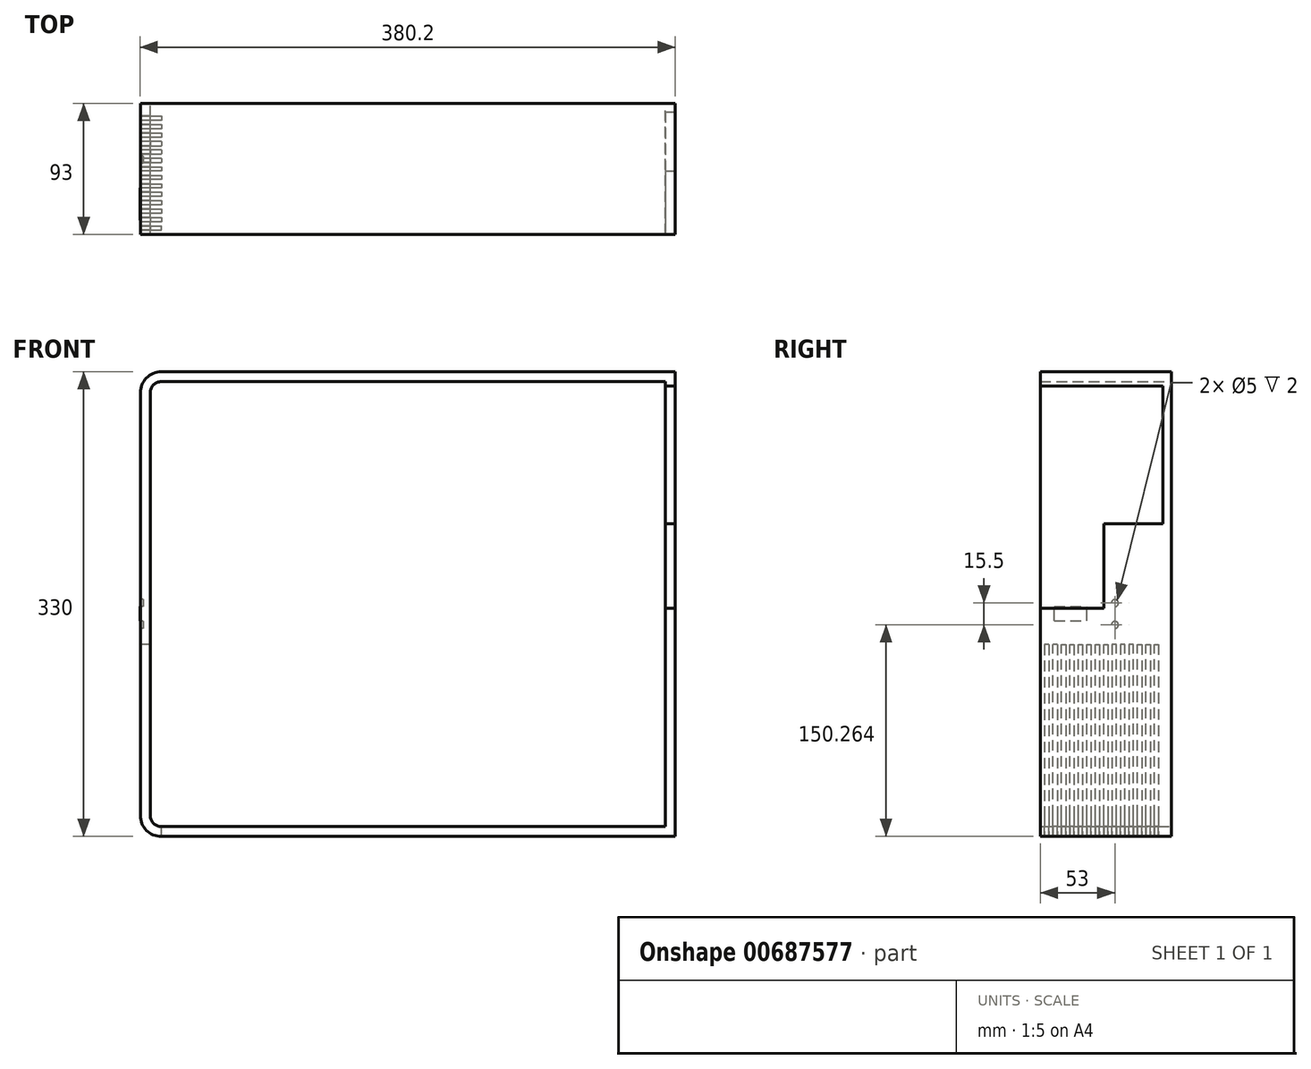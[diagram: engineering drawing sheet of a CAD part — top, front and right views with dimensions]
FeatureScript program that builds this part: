
annotation { "Feature Type Name" : "Feature", "Feature Type Description" : "" }
export const myFeature = defineFeature(function(context is Context, id is Id, definition is map)
    precondition{}
    {
        {
            var Q0;
            Q0=qCreatedBy(makeId("Front.planeOp"),FACE);
            var sketch = newSketch(context, id + "F0", { "sketchPlane" : qUnion([Q0])});
            skLineSegment(sketch, "E0.bottom", {"start": v(-173.8, 236.53) * mm, "end": v(191.2, 236.53) * mm});
            skLineSegment(sketch, "E0.top", {"start": v(-173.8, -93.47) * mm, "end": v(191.2, -93.47) * mm});
            skLineSegment(sketch, "E0.left", {"start": v(-188.8, 221.53) * mm, "end": v(-188.8, -78.47) * mm});
            skLineSegment(sketch, "E0.right", {"start": v(191.2, 236.53) * mm, "end": v(191.2, -93.47) * mm});
            skPoint(sketch, "E1.visualSharp", {"position": v(-188.8, 236.53) * mm});
            skArc(sketch, "E1.filletArc", {"start": v(-186.8, 236.53) * mm, "mid": v(-188.22, 235.95) * mm, "end": v(-188.8, 234.53) * mm});
            skArc(sketch, "E2.filletArc", {"start": v(-173.8, 236.53) * mm, "mid": v(-184.41, 232.14) * mm, "end": v(-188.8, 221.53) * mm});
            skPoint(sketch, "E3.visualSharp", {"position": v(-188.8, -93.47) * mm});
            skArc(sketch, "E3.filletArc", {"start": v(-188.8, -78.47) * mm, "mid": v(-184.41, -89.07) * mm, "end": v(-173.8, -93.47) * mm});
            skArc(sketch, "E4.0", {"start": v(-173.8, 229.53) * mm, "mid": v(-179.46, 227.19) * mm, "end": v(-181.8, 221.53) * mm});
            skLineSegment(sketch, "E4.1", {"start": v(184.2, 229.53) * mm, "end": v(184.2, -86.47) * mm});
            skLineSegment(sketch, "E4.2", {"start": v(-173.8, -86.47) * mm, "end": v(184.2, -86.47) * mm});
            skLineSegment(sketch, "E4.3", {"start": v(-173.8, 229.53) * mm, "end": v(184.2, 229.53) * mm});
            skArc(sketch, "E4.4", {"start": v(-181.8, -78.47) * mm, "mid": v(-179.46, -84.12) * mm, "end": v(-173.8, -86.47) * mm});
            skLineSegment(sketch, "E4.5", {"start": v(-181.8, 221.53) * mm, "end": v(-181.8, -78.47) * mm});
            skSolve(sketch);
        }
        {
            var Q0;
            Q0 = qSketchRegion(id + "F0", true);
            extrude(context, id + "F1", {"entities" : qUnion([Q0]), "depth" : 93 * mm, "offsetDistance" : 25 * mm});
        }
        {
            var Q0;
            Q0=makeQuery(id+"F1.opExtrude","SWEPT_FACE",FACE,{"disambiguationData":[OSD([sQuery(id+"F0.wireOp",EDGE,"E0.right")])]});
            var sketch = newSketch(context, id + "F2", { "sketchPlane" : qUnion([Q0])});
            skLineSegment(sketch, "E5", {"start": v(-6, 226.53) * mm, "end": v(-6, 128.46) * mm});
            skPoint(sketch, "E6.orphan", {"position": v(-6, 236.53) * mm});
            skLineSegment(sketch, "E7", {"start": v(-6, 128.46) * mm, "end": v(-48, 128.46) * mm});
            skLineSegment(sketch, "E8", {"start": v(-48, 128.46) * mm, "end": v(-48, 68.46) * mm});
            skLineSegment(sketch, "E9", {"start": v(-48, 68.46) * mm, "end": v(-93, 68.46) * mm});
            skLineSegment(sketch, "E10", {"start": v(-6, 226.53) * mm, "end": v(-93, 226.53) * mm});
            skSolve(sketch);
        }
        {
            var Q0;
            Q0 = qSketchRegion(id + "F2", true);
            var Q1;
            Q1=makeQuery(id+"F2.imprint","IMPRINT",FACE,{"disambiguationData":[TD([[makeQuery(id+"F2.imprint","IMPRINT",EDGE,{"derivedFrom":sQuery(id+"F2.wireOp",EDGE,"E5")}),-1.0]])]});
            extrude(context, id + "F3", {"entities" : qUnion([Q0, Q1]), "operationType" : NewBodyOperationType.REMOVE, "oppositeDirection" : true, "depth" : 25 * mm, "offsetDistance" : 25 * mm});
        }
        {
            var Q0;
            Q0=makeQuery(id+"F1.opExtrude","SWEPT_FACE",FACE,{"disambiguationData":[OSD([sQuery(id+"F0.wireOp",EDGE,"E0.left")])]});
            var sketch = newSketch(context, id + "F4", { "sketchPlane" : qUnion([Q0])});
            skLineSegment(sketch, "E11", {"start": v(90, -94.2) * mm, "end": v(90, 42.8) * mm});
            skLineSegment(sketch, "E12", {"start": v(87, -94.2) * mm, "end": v(87, 42.8) * mm});
            skLineSegment(sketch, "E13", {"start": v(84, 42.8) * mm, "end": v(84, -94.2) * mm});
            skLineSegment(sketch, "E14", {"start": v(81, -94.2) * mm, "end": v(81, 42.8) * mm});
            skLineSegment(sketch, "E15", {"start": v(78, 42.8) * mm, "end": v(78, -94.2) * mm});
            skLineSegment(sketch, "E16", {"start": v(75, -94.2) * mm, "end": v(75, 42.8) * mm});
            skLineSegment(sketch, "E17", {"start": v(72, 42.8) * mm, "end": v(72, -94.2) * mm});
            skLineSegment(sketch, "E18", {"start": v(69, -94.2) * mm, "end": v(69, 42.8) * mm});
            skLineSegment(sketch, "E19", {"start": v(90, 42.8) * mm, "end": v(87, 42.8) * mm});
            skLineSegment(sketch, "E20", {"start": v(84, 42.8) * mm, "end": v(81, 42.8) * mm});
            skLineSegment(sketch, "E21", {"start": v(90, -94.2) * mm, "end": v(87, -94.2) * mm});
            skLineSegment(sketch, "E22", {"start": v(81, -94.2) * mm, "end": v(84, -94.2) * mm});
            skLineSegment(sketch, "E23", {"start": v(78, -94.2) * mm, "end": v(75, -94.2) * mm});
            skLineSegment(sketch, "E24", {"start": v(72, -94.2) * mm, "end": v(69, -94.2) * mm});
            skLineSegment(sketch, "E25", {"start": v(66, 42.8) * mm, "end": v(66, -94.2) * mm});
            skLineSegment(sketch, "E26", {"start": v(66, -94.2) * mm, "end": v(63, -94.2) * mm});
            skLineSegment(sketch, "E27", {"start": v(63, -94.2) * mm, "end": v(63, 42.8) * mm});
            skLineSegment(sketch, "E28", {"start": v(63, 42.8) * mm, "end": v(66, 42.8) * mm});
            skLineSegment(sketch, "E29", {"start": v(60, 42.8) * mm, "end": v(60, -94.2) * mm});
            skLineSegment(sketch, "E30", {"start": v(60, -94.2) * mm, "end": v(57, -94.2) * mm});
            skLineSegment(sketch, "E31", {"start": v(57, -94.2) * mm, "end": v(57, 42.8) * mm});
            skLineSegment(sketch, "E32", {"start": v(57, 42.8) * mm, "end": v(60, 42.8) * mm});
            skLineSegment(sketch, "E33", {"start": v(54, 42.8) * mm, "end": v(54, -94.2) * mm});
            skLineSegment(sketch, "E34", {"start": v(54, -94.2) * mm, "end": v(51, -94.2) * mm});
            skLineSegment(sketch, "E35", {"start": v(51, -94.2) * mm, "end": v(51, 42.8) * mm});
            skLineSegment(sketch, "E36", {"start": v(51, 42.8) * mm, "end": v(54, 42.8) * mm});
            skLineSegment(sketch, "E37", {"start": v(48, 42.93) * mm, "end": v(48, -94.2) * mm});
            skLineSegment(sketch, "E38", {"start": v(48, -94.2) * mm, "end": v(45, -94.2) * mm});
            skLineSegment(sketch, "E39", {"start": v(45, -94.2) * mm, "end": v(45, 42.93) * mm});
            skLineSegment(sketch, "E40", {"start": v(45, 42.93) * mm, "end": v(48, 42.93) * mm});
            skLineSegment(sketch, "E41", {"start": v(42, 42.93) * mm, "end": v(39, 42.93) * mm});
            skLineSegment(sketch, "E42", {"start": v(39, 42.93) * mm, "end": v(39, -94.2) * mm});
            skLineSegment(sketch, "E43", {"start": v(39, -94.2) * mm, "end": v(42, -94.2) * mm});
            skLineSegment(sketch, "E44", {"start": v(42, -94.2) * mm, "end": v(42, 42.93) * mm});
            skLineSegment(sketch, "E45", {"start": v(36, 42.93) * mm, "end": v(33, 42.93) * mm});
            skLineSegment(sketch, "E46", {"start": v(33, 42.93) * mm, "end": v(33, -94.2) * mm});
            skLineSegment(sketch, "E47", {"start": v(33, -94.2) * mm, "end": v(36, -94.2) * mm});
            skLineSegment(sketch, "E48", {"start": v(36, -94.2) * mm, "end": v(36, 42.93) * mm});
            skLineSegment(sketch, "E49", {"start": v(30, 42.93) * mm, "end": v(27, 42.93) * mm});
            skLineSegment(sketch, "E50", {"start": v(27, 42.93) * mm, "end": v(27, -94.2) * mm});
            skLineSegment(sketch, "E51", {"start": v(27, -94.2) * mm, "end": v(30, -94.2) * mm});
            skLineSegment(sketch, "E52", {"start": v(30, -94.2) * mm, "end": v(30, 42.93) * mm});
            skLineSegment(sketch, "E53", {"start": v(24, 42.93) * mm, "end": v(24, -94.2) * mm});
            skLineSegment(sketch, "E54", {"start": v(24, -94.2) * mm, "end": v(21, -94.2) * mm});
            skLineSegment(sketch, "E55", {"start": v(21, -94.2) * mm, "end": v(21, 42.93) * mm});
            skLineSegment(sketch, "E56", {"start": v(21, 42.93) * mm, "end": v(24, 42.93) * mm});
            skLineSegment(sketch, "E57", {"start": v(18, 42.93) * mm, "end": v(18, -94.2) * mm});
            skLineSegment(sketch, "E58", {"start": v(18, -94.2) * mm, "end": v(15, -94.2) * mm});
            skLineSegment(sketch, "E59", {"start": v(15, -94.2) * mm, "end": v(15, 42.93) * mm});
            skLineSegment(sketch, "E60", {"start": v(15, 42.93) * mm, "end": v(18, 42.93) * mm});
            skLineSegment(sketch, "E61", {"start": v(12, 42.93) * mm, "end": v(12, -94.2) * mm});
            skLineSegment(sketch, "E62", {"start": v(12, -94.2) * mm, "end": v(9, -94.2) * mm});
            skLineSegment(sketch, "E63", {"start": v(9, -94.2) * mm, "end": v(9, 42.93) * mm});
            skLineSegment(sketch, "E64", {"start": v(9, 42.93) * mm, "end": v(12, 42.93) * mm});
            skLineSegment(sketch, "E65", {"start": v(69, 42.8) * mm, "end": v(72, 42.8) * mm});
            skLineSegment(sketch, "E66", {"start": v(75, 42.8) * mm, "end": v(78, 42.8) * mm});
            skSolve(sketch);
        }
        {
            var Q0;
            {var subQ0=sQuery(id+"F4.wireOp",EDGE,"E21");Q0=makeQuery(id+"F4.imprint","IMPRINT",FACE,{"disambiguationData":[TD([[makeQuery(id+"F4.imprint","IMPRINT",EDGE,{"derivedFrom":subQ0}),-1.0]])]});}
            var Q1;
            {var subQ0=sQuery(id+"F4.wireOp",EDGE,"E19");Q1=makeQuery(id+"F4.imprint","IMPRINT",FACE,{"disambiguationData":[TD([[makeQuery(id+"F4.imprint","IMPRINT",EDGE,{"derivedFrom":subQ0}),1.0]])]});}
            extrude(context, id + "F5", {"entities" : qUnion([Q0, Q1]), "operationType" : NewBodyOperationType.REMOVE, "oppositeDirection" : true, "depth" : 15 * mm, "offsetDistance" : 25 * mm});
        }
        {
            var Q0;
            {var subQ0=sQuery(id+"F4.wireOp",EDGE,"E20");Q0=makeQuery(id+"F4.imprint","IMPRINT",FACE,{"disambiguationData":[TD([[makeQuery(id+"F4.imprint","IMPRINT",EDGE,{"derivedFrom":subQ0}),1.0]])]});}
            var Q1;
            {var subQ0=sQuery(id+"F4.wireOp",EDGE,"E22");Q1=makeQuery(id+"F4.imprint","IMPRINT",FACE,{"disambiguationData":[TD([[makeQuery(id+"F4.imprint","IMPRINT",EDGE,{"derivedFrom":subQ0}),1.0]])]});}
            extrude(context, id + "F6", {"entities" : qUnion([Q0, Q1]), "operationType" : NewBodyOperationType.REMOVE, "oppositeDirection" : true, "depth" : 15 * mm, "offsetDistance" : 25 * mm});
        }
        {
            var Q0;
            {var subQ0=sQuery(id+"F4.wireOp",EDGE,"E66");Q0=makeQuery(id+"F4.imprint","IMPRINT",FACE,{"disambiguationData":[TD([[makeQuery(id+"F4.imprint","IMPRINT",EDGE,{"derivedFrom":subQ0}),-1.0]])]});}
            var Q1;
            {var subQ0=sQuery(id+"F4.wireOp",EDGE,"E23");Q1=makeQuery(id+"F4.imprint","IMPRINT",FACE,{"disambiguationData":[TD([[makeQuery(id+"F4.imprint","IMPRINT",EDGE,{"derivedFrom":subQ0}),-1.0]])]});}
            extrude(context, id + "F7", {"entities" : qUnion([Q0, Q1]), "operationType" : NewBodyOperationType.REMOVE, "oppositeDirection" : true, "depth" : 15 * mm, "offsetDistance" : 25 * mm});
        }
        {
            var Q0;
            {var subQ0=sQuery(id+"F4.wireOp",EDGE,"E65");Q0=makeQuery(id+"F4.imprint","IMPRINT",FACE,{"disambiguationData":[TD([[makeQuery(id+"F4.imprint","IMPRINT",EDGE,{"derivedFrom":subQ0}),-1.0]])]});}
            var Q1;
            {var subQ0=sQuery(id+"F4.wireOp",EDGE,"E24");Q1=makeQuery(id+"F4.imprint","IMPRINT",FACE,{"disambiguationData":[TD([[makeQuery(id+"F4.imprint","IMPRINT",EDGE,{"derivedFrom":subQ0}),-1.0]])]});}
            extrude(context, id + "F8", {"entities" : qUnion([Q0, Q1]), "operationType" : NewBodyOperationType.REMOVE, "oppositeDirection" : true, "depth" : 15 * mm, "offsetDistance" : 25 * mm});
        }
        {
            var Q0;
            {var subQ0=sQuery(id+"F4.wireOp",EDGE,"E28");Q0=makeQuery(id+"F4.imprint","IMPRINT",FACE,{"disambiguationData":[TD([[makeQuery(id+"F4.imprint","IMPRINT",EDGE,{"derivedFrom":subQ0}),-1.0]])]});}
            var Q1;
            {var subQ0=sQuery(id+"F4.wireOp",EDGE,"E26");Q1=makeQuery(id+"F4.imprint","IMPRINT",FACE,{"disambiguationData":[TD([[makeQuery(id+"F4.imprint","IMPRINT",EDGE,{"derivedFrom":subQ0}),-1.0]])]});}
            extrude(context, id + "F9", {"entities" : qUnion([Q0, Q1]), "operationType" : NewBodyOperationType.REMOVE, "oppositeDirection" : true, "depth" : 15 * mm, "offsetDistance" : 25 * mm});
        }
        {
            var Q0;
            {var subQ0=sQuery(id+"F4.wireOp",EDGE,"E30");Q0=makeQuery(id+"F4.imprint","IMPRINT",FACE,{"disambiguationData":[TD([[makeQuery(id+"F4.imprint","IMPRINT",EDGE,{"derivedFrom":subQ0}),-1.0]])]});}
            var Q1;
            {var subQ0=sQuery(id+"F4.wireOp",EDGE,"E32");Q1=makeQuery(id+"F4.imprint","IMPRINT",FACE,{"disambiguationData":[TD([[makeQuery(id+"F4.imprint","IMPRINT",EDGE,{"derivedFrom":subQ0}),-1.0]])]});}
            extrude(context, id + "F10", {"entities" : qUnion([Q0, Q1]), "operationType" : NewBodyOperationType.REMOVE, "oppositeDirection" : true, "depth" : 15 * mm, "offsetDistance" : 25 * mm});
        }
        {
            var Q0;
            {var subQ0=sQuery(id+"F4.wireOp",EDGE,"E36");Q0=makeQuery(id+"F4.imprint","IMPRINT",FACE,{"disambiguationData":[TD([[makeQuery(id+"F4.imprint","IMPRINT",EDGE,{"derivedFrom":subQ0}),-1.0]])]});}
            var Q1;
            {var subQ0=sQuery(id+"F4.wireOp",EDGE,"E34");Q1=makeQuery(id+"F4.imprint","IMPRINT",FACE,{"disambiguationData":[TD([[makeQuery(id+"F4.imprint","IMPRINT",EDGE,{"derivedFrom":subQ0}),-1.0]])]});}
            extrude(context, id + "F11", {"entities" : qUnion([Q0, Q1]), "operationType" : NewBodyOperationType.REMOVE, "oppositeDirection" : true, "depth" : 15 * mm, "offsetDistance" : 25 * mm});
        }
        {
            var Q0;
            {var subQ0=sQuery(id+"F4.wireOp",EDGE,"E38");Q0=makeQuery(id+"F4.imprint","IMPRINT",FACE,{"disambiguationData":[TD([[makeQuery(id+"F4.imprint","IMPRINT",EDGE,{"derivedFrom":subQ0}),-1.0]])]});}
            var Q1;
            {var subQ0=sQuery(id+"F4.wireOp",EDGE,"E40");Q1=makeQuery(id+"F4.imprint","IMPRINT",FACE,{"disambiguationData":[TD([[makeQuery(id+"F4.imprint","IMPRINT",EDGE,{"derivedFrom":subQ0}),-1.0]])]});}
            extrude(context, id + "F12", {"entities" : qUnion([Q0, Q1]), "operationType" : NewBodyOperationType.REMOVE, "oppositeDirection" : true, "depth" : 15 * mm, "offsetDistance" : 25 * mm});
        }
        {
            var Q0;
            {var subQ0=sQuery(id+"F4.wireOp",EDGE,"E41");Q0=makeQuery(id+"F4.imprint","IMPRINT",FACE,{"disambiguationData":[TD([[makeQuery(id+"F4.imprint","IMPRINT",EDGE,{"derivedFrom":subQ0}),1.0]])]});}
            var Q1;
            {var subQ0=sQuery(id+"F4.wireOp",EDGE,"E43");Q1=makeQuery(id+"F4.imprint","IMPRINT",FACE,{"disambiguationData":[TD([[makeQuery(id+"F4.imprint","IMPRINT",EDGE,{"derivedFrom":subQ0}),1.0]])]});}
            extrude(context, id + "F13", {"entities" : qUnion([Q0, Q1]), "operationType" : NewBodyOperationType.REMOVE, "oppositeDirection" : true, "depth" : 15 * mm, "offsetDistance" : 25 * mm});
        }
        {
            var Q0;
            {var subQ0=sQuery(id+"F4.wireOp",EDGE,"E41");Q0=makeQuery(id+"F4.imprint","IMPRINT",FACE,{"disambiguationData":[TD([[makeQuery(id+"F4.imprint","IMPRINT",EDGE,{"derivedFrom":subQ0}),1.0]])]});}
            var Q1;
            {var subQ0=sQuery(id+"F4.wireOp",EDGE,"E43");Q1=makeQuery(id+"F4.imprint","IMPRINT",FACE,{"disambiguationData":[TD([[makeQuery(id+"F4.imprint","IMPRINT",EDGE,{"derivedFrom":subQ0}),1.0]])]});}
            extrude(context, id + "F14", {"entities" : qUnion([Q0, Q1]), "operationType" : NewBodyOperationType.REMOVE, "oppositeDirection" : true, "depth" : 15 * mm, "offsetDistance" : 25 * mm});
        }
        {
            var Q0;
            {var subQ0=sQuery(id+"F4.wireOp",EDGE,"E45");Q0=makeQuery(id+"F4.imprint","IMPRINT",FACE,{"disambiguationData":[TD([[makeQuery(id+"F4.imprint","IMPRINT",EDGE,{"derivedFrom":subQ0}),1.0]])]});}
            var Q1;
            {var subQ0=sQuery(id+"F4.wireOp",EDGE,"E47");Q1=makeQuery(id+"F4.imprint","IMPRINT",FACE,{"disambiguationData":[TD([[makeQuery(id+"F4.imprint","IMPRINT",EDGE,{"derivedFrom":subQ0}),1.0]])]});}
            extrude(context, id + "F15", {"entities" : qUnion([Q0, Q1]), "operationType" : NewBodyOperationType.REMOVE, "oppositeDirection" : true, "depth" : 15 * mm, "offsetDistance" : 25 * mm});
        }
        {
            var Q0;
            {var subQ0=sQuery(id+"F4.wireOp",EDGE,"E49");Q0=makeQuery(id+"F4.imprint","IMPRINT",FACE,{"disambiguationData":[TD([[makeQuery(id+"F4.imprint","IMPRINT",EDGE,{"derivedFrom":subQ0}),1.0]])]});}
            var Q1;
            {var subQ0=sQuery(id+"F4.wireOp",EDGE,"E51");Q1=makeQuery(id+"F4.imprint","IMPRINT",FACE,{"disambiguationData":[TD([[makeQuery(id+"F4.imprint","IMPRINT",EDGE,{"derivedFrom":subQ0}),1.0]])]});}
            extrude(context, id + "F16", {"entities" : qUnion([Q0, Q1]), "operationType" : NewBodyOperationType.REMOVE, "oppositeDirection" : true, "depth" : 15 * mm, "offsetDistance" : 25 * mm});
        }
        {
            var Q0;
            {var subQ0=sQuery(id+"F4.wireOp",EDGE,"E56");Q0=makeQuery(id+"F4.imprint","IMPRINT",FACE,{"disambiguationData":[TD([[makeQuery(id+"F4.imprint","IMPRINT",EDGE,{"derivedFrom":subQ0}),-1.0]])]});}
            var Q1;
            {var subQ0=sQuery(id+"F4.wireOp",EDGE,"E54");Q1=makeQuery(id+"F4.imprint","IMPRINT",FACE,{"disambiguationData":[TD([[makeQuery(id+"F4.imprint","IMPRINT",EDGE,{"derivedFrom":subQ0}),-1.0]])]});}
            extrude(context, id + "F17", {"entities" : qUnion([Q0, Q1]), "operationType" : NewBodyOperationType.REMOVE, "oppositeDirection" : true, "depth" : 15 * mm, "offsetDistance" : 25 * mm});
        }
        {
            var Q0;
            {var subQ0=sQuery(id+"F4.wireOp",EDGE,"E60");Q0=makeQuery(id+"F4.imprint","IMPRINT",FACE,{"disambiguationData":[TD([[makeQuery(id+"F4.imprint","IMPRINT",EDGE,{"derivedFrom":subQ0}),-1.0]])]});}
            var Q1;
            {var subQ0=sQuery(id+"F4.wireOp",EDGE,"E58");Q1=makeQuery(id+"F4.imprint","IMPRINT",FACE,{"disambiguationData":[TD([[makeQuery(id+"F4.imprint","IMPRINT",EDGE,{"derivedFrom":subQ0}),-1.0]])]});}
            extrude(context, id + "F18", {"entities" : qUnion([Q0, Q1]), "operationType" : NewBodyOperationType.REMOVE, "oppositeDirection" : true, "depth" : 15 * mm, "offsetDistance" : 25 * mm});
        }
        {
            var Q0;
            {var subQ0=sQuery(id+"F4.wireOp",EDGE,"E64");Q0=makeQuery(id+"F4.imprint","IMPRINT",FACE,{"disambiguationData":[TD([[makeQuery(id+"F4.imprint","IMPRINT",EDGE,{"derivedFrom":subQ0}),-1.0]])]});}
            var Q1;
            {var subQ0=sQuery(id+"F4.wireOp",EDGE,"E62");Q1=makeQuery(id+"F4.imprint","IMPRINT",FACE,{"disambiguationData":[TD([[makeQuery(id+"F4.imprint","IMPRINT",EDGE,{"derivedFrom":subQ0}),-1.0]])]});}
            extrude(context, id + "F19", {"entities" : qUnion([Q0, Q1]), "operationType" : NewBodyOperationType.REMOVE, "oppositeDirection" : true, "depth" : 15 * mm, "offsetDistance" : 25 * mm});
        }
        {
            var Q0;
            Q0=makeQuery(id+"F1.opExtrude","SWEPT_FACE",FACE,{"disambiguationData":[OSD([sQuery(id+"F0.wireOp",EDGE,"E0.left")])]});
            var sketch = newSketch(context, id + "F20", { "sketchPlane" : qUnion([Q0])});
            skLineSegment(sketch, "E67.bottom", {"start": v(83, 59.8) * mm, "end": v(60, 59.8) * mm});
            skLineSegment(sketch, "E67.top", {"start": v(83, 69.8) * mm, "end": v(60, 69.8) * mm});
            skLineSegment(sketch, "E67.left", {"start": v(83, 59.8) * mm, "end": v(83, 69.8) * mm});
            skLineSegment(sketch, "E67.right", {"start": v(60, 59.8) * mm, "end": v(60, 69.8) * mm});
            skSolve(sketch);
        }
        {
            var Q0;
            Q0 = qSketchRegion(id + "F20", true);
            extrude(context, id + "F21", {"entities" : qUnion([Q0]), "operationType" : NewBodyOperationType.ADD, "depth" : 0.2 * mm, "offsetDistance" : 25 * mm});
        }
        {
            var Q0;
            Q0=makeQuery(id+"F1.opExtrude","SWEPT_FACE",FACE,{"disambiguationData":[OSD([sQuery(id+"F0.wireOp",EDGE,"E0.left")])]});
            var sketch = newSketch(context, id + "F22", { "sketchPlane" : qUnion([Q0])});
            skPoint(sketch, "E68.startSnap0", {"position": v(60, 64.8) * mm});
            skCircle(sketch, "E69", {"center": v(40, 72.3) * mm, "radius": 2.5 * mm});
            skCircle(sketch, "E70", {"center": v(40, 56.8) * mm, "radius": 2.5 * mm});
            skSolve(sketch);
        }
        {
            var Q0;
            Q0=makeQuery(id+"F22.imprint","IMPRINT",FACE,{"disambiguationData":[TD([[makeQuery(id+"F22.imprint","IMPRINT",EDGE,{"derivedFrom":sQuery(id+"F22.wireOp",EDGE,"E70")}),1.0]])]});
            extrude(context, id + "F23", {"entities" : qUnion([Q0]), "operationType" : NewBodyOperationType.REMOVE, "oppositeDirection" : true, "depth" : 2 * mm, "offsetDistance" : 25 * mm});
        }
        {
            var Q0;
            Q0=makeQuery(id+"F22.imprint","IMPRINT",FACE,{"disambiguationData":[TD([[makeQuery(id+"F22.imprint","IMPRINT",EDGE,{"derivedFrom":sQuery(id+"F22.wireOp",EDGE,"E69")}),1.0]])]});
            extrude(context, id + "F24", {"entities" : qUnion([Q0]), "operationType" : NewBodyOperationType.REMOVE, "oppositeDirection" : true, "depth" : 2 * mm, "offsetDistance" : 25 * mm});
        }
    });
